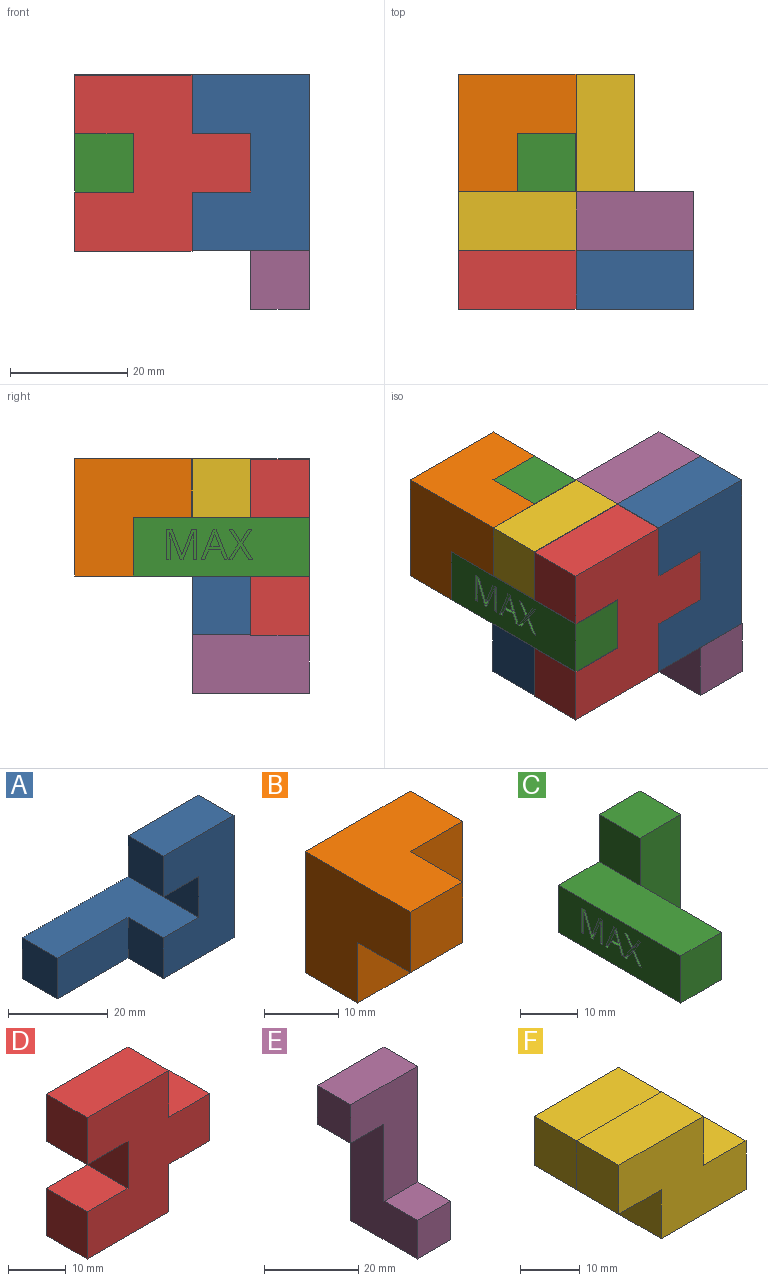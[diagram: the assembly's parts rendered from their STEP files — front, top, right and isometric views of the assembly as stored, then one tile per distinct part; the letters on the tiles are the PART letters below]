
ASSEMBLY  parts=6 mates=5
PART A: 14 faces, bbox 40x20x30 mm
  f0: plane 10x10mm, normal (-1,0,0), area 100mm2, adj f3,f8,f9,f12
  f1: plane 30x20mm, normal (0,1,0), area 400mm2, adj f2,f4,f5,f6,f7,f8,f10
  f2: plane 20x10mm, normal (0,0,1), area 200mm2, adj f1,f3,f5,f6
  f3: plane 30x20mm, normal (0,-1,0), area 500mm2, adj f0,f2,f4,f5,f6,f7,f8,f9
  f4: plane 10x10mm, normal (0,0,-1), area 100mm2, adj f1,f3,f6,f7
  f5: plane 30x10mm, normal (1,0,0), area 300mm2, adj f1,f2,f3,f8
  f6: plane 10x10mm, normal (-1,0,0), area 100mm2, adj f1,f2,f3,f4
  f7: plane 10x10mm, normal (-1,0,0), area 100mm2, adj f1,f3,f4,f9
  f8: plane 40x20mm, normal (0,0,-1), area 500mm2, adj f0,f1,f3,f5,f10,f11,f12,f13
  f9: plane 30x20mm, normal (0,0,1), area 400mm2, adj f0,f3,f7,f10,f11,f12,f13
  f10: plane 10x10mm, normal (1,0,0), area 100mm2, adj f1,f8,f9,f11
  f11: plane 30x10mm, normal (0,1,0), area 300mm2, adj f8,f9,f10,f13
  f12: plane 20x10mm, normal (0,-1,0), area 200mm2, adj f0,f8,f9,f13
  f13: plane 10x10mm, normal (-1,0,0), area 100mm2, adj f8,f9,f11,f12
PART B: 12 faces, bbox 20x20x20 mm
  f0: plane 10x10mm, normal (0,0,-1), area 100mm2, adj f6,f7,f8,f9
  f1: plane 20x20mm, normal (0,0,1), area 300mm2, adj f2,f4,f5,f6,f7,f8
  f2: plane 20x20mm, normal (-1,0,0), area 300mm2, adj f1,f3,f5,f6,f10,f11
  f3: plane 10x10mm, normal (0,0,-1), area 100mm2, adj f2,f4,f5,f10
  f4: plane 10x10mm, normal (1,0,0), area 100mm2, adj f1,f3,f5,f7
  f5: plane 10x10mm, normal (0,-1,0), area 100mm2, adj f1,f2,f3,f4
  f6: plane 20x20mm, normal (0,1,0), area 300mm2, adj f0,f1,f2,f8,f9,f11
  f7: plane 10x10mm, normal (0,-1,0), area 100mm2, adj f0,f1,f4,f8
  f8: plane 10x10mm, normal (1,0,0), area 100mm2, adj f0,f1,f6,f7
  f9: plane 10x10mm, normal (1,0,0), area 100mm2, adj f0,f6,f10,f11
  f10: plane 10x10mm, normal (0,-1,0), area 100mm2, adj f2,f3,f9,f11
  f11: plane 10x10mm, normal (0,0,-1), area 100mm2, adj f2,f6,f9,f10
PART C: 57 faces, bbox 20x30x20 mm
  f0: plane 30x10mm, normal (-1,0,0), area 273.3mm2, adj f5,f6,f7,f9,f14,f15,f16,f17
  f1: plane 20x10mm, normal (0,-1,0), area 200mm2, adj f2,f3,f4,f6,f8
  f2: plane 10x10mm, normal (-1,0,0), area 100mm2, adj f1,f3,f5,f7
  f3: plane 10x10mm, normal (0,0,1), area 100mm2, adj f1,f2,f4,f5
  f4: plane 20x10mm, normal (1,0,0), area 200mm2, adj f1,f3,f5,f6
  f5: plane 20x20mm, normal (0,1,0), area 300mm2, adj f0,f2,f3,f4,f6,f7
  f6: plane 30x20mm, normal (0,0,-1), area 400mm2, adj f0,f1,f4,f5,f8,f9
  f7: plane 30x10mm, normal (0,0,1), area 300mm2, adj f0,f2,f5,f8,f9
  f8: plane 20x10mm, normal (1,0,0), area 200mm2, adj f1,f6,f7,f9
  f9: plane 10x10mm, normal (0,-1,0), area 100mm2, adj f0,f6,f7,f8
  f10: plane 1.61x1mm, normal (0,-0.94,0.35), area 1.7mm2, adj f11,f22,f23,f56
  f11: plane 1.68x1mm, normal (0,0,-1), area 1.7mm2, adj f10,f12,f23,f56
  f12: plane 1.61x1mm, normal (0,0.94,0.35), area 1.7mm2, adj f11,f13,f23,f56
  f13: extruded ~1x0.75mm, area 0.8mm2, adj f12,f22,f23,f56
  f14: plane 1.65x1mm, normal (0,-0.93,0.36), area 1.8mm2, adj f0,f15,f21,f23
  f15: plane 1x0.63mm, normal (0,0,1), area 0.6mm2, adj f0,f14,f16,f23
  f16: plane 5.22x2.04mm, normal (0,0.93,-0.36), area 5.6mm2, adj f0,f15,f17,f23
  f17: plane 1x0.51mm, normal (0,0,-1), area 0.5mm2, adj f0,f16,f18,f23
  f18: plane 5.22x2.05mm, normal (0,-0.93,-0.37), area 5.6mm2, adj f0,f17,f19,f23
  f19: plane 1x0.61mm, normal (0,0,1), area 0.6mm2, adj f0,f18,f20,f23
  f20: plane 1.65x1mm, normal (0,0.93,0.36), area 1.8mm2, adj f0,f19,f21,f23
  f21: plane 2.08x1mm, normal (0,0,1), area 2.1mm2, adj f0,f14,f20,f23
  f22: extruded ~1x0.75mm, area 0.8mm2, adj f10,f13,f23,f56
  f23: plane 5.22x4.61mm, normal (-1,0,0), area 6.9mm2, adj f10,f11,f12,f13,f14,f15,f16,f17
  f24: plane 1x0.69mm, normal (0,0,1), area 0.7mm2, adj f0,f25,f35,f36
  f25: plane 2.74x1.73mm, normal (0,0.84,-0.54), area 3.2mm2, adj f0,f24,f26,f36
  f26: plane 2.46x1.61mm, normal (0,0.84,0.55), area 2.9mm2, adj f0,f25,f27,f36
  f27: plane 1x0.64mm, normal (0,0,-1), area 0.6mm2, adj f0,f26,f28,f36
  f28: plane 2.06x1.3mm, normal (0,-0.85,-0.53), area 2.4mm2, adj f0,f27,f29,f36
  f29: plane 2.06x1.29mm, normal (0,0.85,-0.53), area 2.4mm2, adj f0,f28,f30,f36
  f30: plane 1x0.67mm, normal (0,0,-1), area 0.7mm2, adj f0,f29,f31,f36
  f31: plane 2.48x1.61mm, normal (0,-0.84,0.54), area 3mm2, adj f0,f30,f32,f36
  f32: plane 2.72x1.73mm, normal (0,-0.84,-0.54), area 3.2mm2, adj f0,f31,f33,f36
  f33: plane 1x0.64mm, normal (0,0,1), area 0.6mm2, adj f0,f32,f34,f36
  f34: plane 2.28x1.42mm, normal (0,0.85,0.53), area 2.7mm2, adj f0,f33,f35,f36
  f35: plane 2.28x1.4mm, normal (0,-0.85,0.52), area 2.7mm2, adj f0,f24,f34,f36
  f36: plane 5.2x4.14mm, normal (-1,0,0), area 6.4mm2, adj f24,f25,f26,f27,f28,f29,f30,f31
  f37: plane 4.61x1.76mm, normal (0,-0.93,0.36), area 4.9mm2, adj f0,f38,f54,f55
  f38: plane 1x0.49mm, normal (0,0,1), area 0.5mm2, adj f0,f37,f39,f55
  f39: plane 4.6x1.78mm, normal (0,0.93,0.36), area 4.9mm2, adj f0,f38,f40,f55
  f40: plane 1x0.03mm, normal (0,0,1), area 0mm2, adj f0,f39,f41,f55
  f41: extruded ~1.25x1mm, area 1.3mm2, adj f0,f40,f42,f55
  f42: plane 3.35x1mm, normal (0,-1,0), area 3.3mm2, adj f0,f41,f43,f55
  f43: plane 1x0.6mm, normal (0,0,1), area 0.6mm2, adj f0,f42,f44,f55
  f44: plane 5.2x1mm, normal (0,1,0), area 5.2mm2, adj f0,f43,f45,f55
  f45: plane 1x0.9mm, normal (0,0,-1), area 0.9mm2, adj f0,f44,f46,f55
  f46: plane 4.29x1.66mm, normal (0,-0.93,-0.36), area 4.6mm2, adj f0,f45,f47,f55
  f47: plane 1x0.03mm, normal (0,0,-1), area 0mm2, adj f0,f46,f48,f55
  f48: plane 4.29x1.65mm, normal (0,0.93,-0.36), area 4.6mm2, adj f0,f47,f49,f55
  f49: plane 1x0.91mm, normal (0,0,-1), area 0.9mm2, adj f0,f48,f50,f55
  f50: plane 5.2x1mm, normal (0,-1,0), area 5.2mm2, adj f0,f49,f51,f55
  f51: plane 1x0.56mm, normal (0,0,1), area 0.6mm2, adj f0,f50,f52,f55
  f52: plane 3.3x1mm, normal (0,1,0), area 3.3mm2, adj f0,f51,f53,f55
  f53: extruded ~1.3x1mm, area 1.3mm2, adj f0,f52,f54,f55
  f54: plane 1x0.03mm, normal (0,0,1), area 0mm2, adj f0,f37,f53,f55
  f55: plane 5.2x5.15mm, normal (-1,0,0), area 11.5mm2, adj f37,f38,f39,f40,f41,f42,f43,f44
  f56: plane 2.36x1.68mm, normal (-1,0,0), area 1.9mm2, adj f10,f11,f12,f13,f22
PART D: 14 faces, bbox 30x10x30 mm
  f0: plane 10.1x10mm, normal (1,0,0), area 101mm2, adj f3,f5,f8,f11
  f1: plane 10x9.9mm, normal (1,0,0), area 99mm2, adj f3,f4,f5,f12
  f2: plane 10x10mm, normal (-1,0,0), area 100mm2, adj f3,f5,f6,f9
  f3: plane 30x30mm, normal (0,1,0), area 600mm2, adj f0,f1,f2,f4,f6,f7,f8,f9
  f4: plane 20x10mm, normal (0,0,1), area 200mm2, adj f1,f3,f5,f7
  f5: plane 30x30mm, normal (0,-1,0), area 600mm2, adj f0,f1,f2,f4,f6,f7,f8,f9
  f6: plane 10x10mm, normal (0,0,-1), area 100mm2, adj f2,f3,f5,f7
  f7: plane 10x10mm, normal (-1,0,0), area 100mm2, adj f3,f4,f5,f6
  f8: plane 20x10mm, normal (0,0,-1), area 200mm2, adj f0,f3,f5,f10
  f9: plane 10x10mm, normal (0,0,1), area 100mm2, adj f2,f3,f5,f10
  f10: plane 10x10mm, normal (-1,0,0), area 100mm2, adj f3,f5,f8,f9
  f11: plane 10x10mm, normal (0,0,-1), area 100mm2, adj f0,f3,f5,f13
  f12: plane 10x10mm, normal (0,0,1), area 100mm2, adj f1,f3,f5,f13
  f13: plane 10x10mm, normal (1,0,0), area 100mm2, adj f3,f5,f11,f12
PART E: 10 faces, bbox 20x20x40 mm
  f0: plane 30x20mm, normal (0,-1,0), area 400mm2, adj f1,f2,f4,f5,f6,f8
  f1: plane 10x10mm, normal (0,0,-1), area 100mm2, adj f0,f3,f5,f6
  f2: plane 20x10mm, normal (0,0,1), area 200mm2, adj f0,f3,f4,f5
  f3: plane 40x20mm, normal (0,1,0), area 500mm2, adj f1,f2,f4,f5,f6,f7
  f4: plane 40x20mm, normal (1,0,0), area 500mm2, adj f0,f2,f3,f7,f8,f9
  f5: plane 10x10mm, normal (-1,0,0), area 100mm2, adj f0,f1,f2,f3
  f6: plane 30x20mm, normal (-1,0,0), area 400mm2, adj f0,f1,f3,f7,f8,f9
  f7: plane 20x10mm, normal (0,0,-1), area 200mm2, adj f3,f4,f6,f9
  f8: plane 10x10mm, normal (0,0,1), area 100mm2, adj f0,f4,f6,f9
  f9: plane 10x10mm, normal (0,-1,0), area 100mm2, adj f4,f6,f7,f8
PART F: 14 faces, bbox 30x30x20 mm
  f0: plane 30x20mm, normal (0,0,1), area 400mm2, adj f1,f2,f3,f5,f6,f7,f10
  f1: plane 10x10mm, normal (-1,0,0), area 100mm2, adj f0,f3,f4,f8
  f2: plane 20x10mm, normal (0,1,0), area 200mm2, adj f0,f4,f5,f6
  f3: plane 10x10mm, normal (0,-1,0), area 100mm2, adj f0,f1,f4,f6
  f4: plane 30x20mm, normal (0,0,-1), area 500mm2, adj f1,f2,f3,f5,f6,f7,f8,f9
  f5: plane 30x10mm, normal (1,0,0), area 300mm2, adj f0,f2,f4,f7
  f6: plane 10x10mm, normal (-1,0,0), area 100mm2, adj f0,f2,f3,f4
  f7: plane 30x20mm, normal (0,-1,0), area 400mm2, adj f0,f4,f5,f9,f10,f11,f12,f13
  f8: plane 20x20mm, normal (0,1,0), area 300mm2, adj f1,f4,f9,f10,f11,f12,f13
  f9: plane 10x10mm, normal (-1,0,0), area 100mm2, adj f4,f7,f8,f12
  f10: plane 10x10mm, normal (1,0,0), area 100mm2, adj f0,f7,f8,f11
  f11: plane 20x10mm, normal (0,0,1), area 200mm2, adj f7,f8,f10,f13
  f12: plane 10x10mm, normal (0,0,-1), area 100mm2, adj f7,f8,f9,f13
  f13: plane 10x10mm, normal (-1,0,0), area 100mm2, adj f7,f8,f11,f12
PLACE A t=(-36,-78.98,-13.21)mm
PLACE B t=(-3.1,-6.96,-15.61)mm
PLACE C t=(-16.94,-16.96,-4.24)mm
PLACE D t=(-56,-71.28,-13.2)mm
PLACE E t=(-36,-0.12,-28.76)mm
PLACE F t=(-46,-59.4,-27.63)mm
MATE fastened D.f11 <-> A.f9  axis (0,0,-1) through (-36,-46.96,1.67)mm
MATE fastened B.f5 <-> F.f8  axis (0,-1,0) through (-56,-26.96,21.67)mm
MATE fastened F.f10 <-> E.f5  axis (1,0,0) through (-36,-31.96,21.67)mm
MATE fastened E.f0 <-> A.f1  axis (0,-1,0) through (-16,-36.96,21.67)mm
MATE fastened C.f1 <-> F.f8  axis (0,-1,0) through (-36,-26.96,21.67)mm
